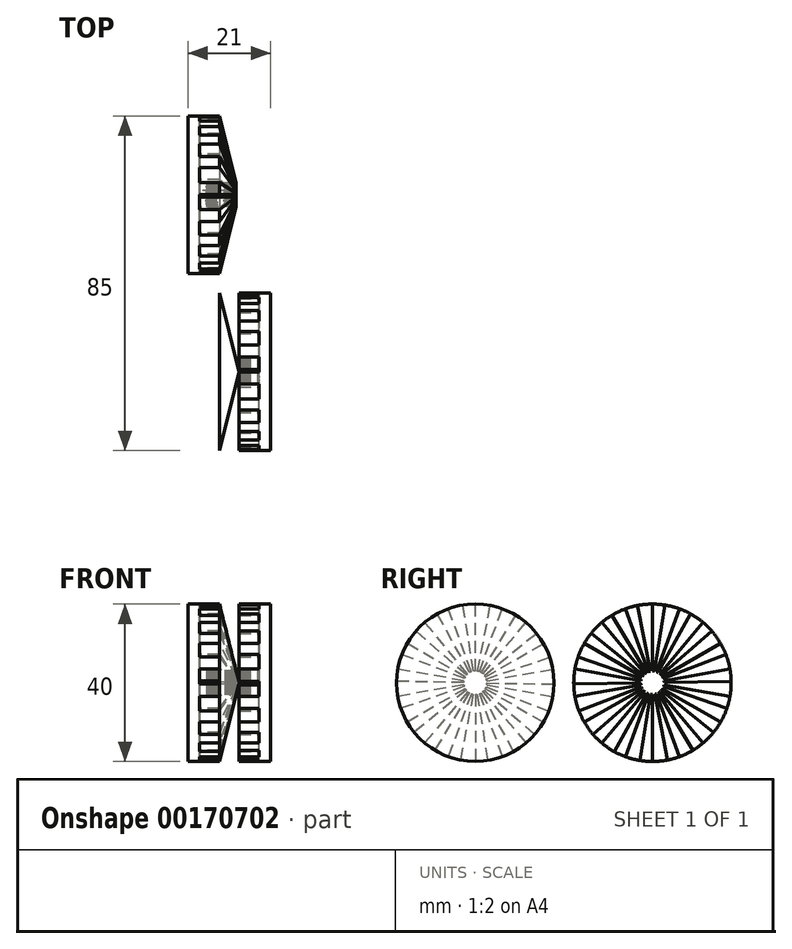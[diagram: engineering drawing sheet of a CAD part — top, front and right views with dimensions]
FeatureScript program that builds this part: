
annotation { "Feature Type Name" : "Feature", "Feature Type Description" : "" }
export const myFeature = defineFeature(function(context is Context, id is Id, definition is map)
    precondition{}
    {
        {
            var Q0;
            Q0=qCreatedBy(makeId("Front.planeOp"),FACE);
            var sketch = newSketch(context, id + "F0", { "sketchPlane" : qUnion([Q0])});
            skLineSegment(sketch, "E0", {"start": v(0, 20) * mm, "end": v(0, 0) * mm});
            skLineSegment(sketch, "E1", {"start": v(0, 0) * mm, "end": v(10, 0) * mm});
            skLineSegment(sketch, "E2", {"start": v(10, 0) * mm, "end": v(5, 20) * mm});
            skLineSegment(sketch, "E3", {"start": v(5, 20) * mm, "end": v(0, 20) * mm});
            skLineSegment(sketch, "E4", {"start": v(5, 20) * mm, "end": v(5, 0) * mm, "construction": true});
            skSolve(sketch);
        }
        {
            var Q0;
            Q0 = qSketchRegion(id + "F0", true);
            var Q1;
            Q1=sQuery(id+"F0.wireOp",EDGE,"E1");
            revolve(context, id + "F1", {"entities" : qUnion([Q0]), "axis" : qUnion([Q1]), "revolveType" : RevolveType.FULL});
        }
        {
            var Q0;
            Q0=qCreatedBy(makeId("Front.planeOp"),FACE);
            cPlane(context, id + "F2", {"entities" : qUnion([Q0]), "cplaneType" : CPlaneType.OFFSET, "offset" : 45 * mm, "width" : 150 * mm, "height" : 150 * mm});
        }
        {
            var Q0;
            Q0=qCreatedBy(id+"F2.planeOp",FACE);
            var sketch = newSketch(context, id + "F3", { "sketchPlane" : qUnion([Q0])});
            skLineSegment(sketch, "E5", {"start": v(15, 0) * mm, "end": v(15, 20) * mm});
            skLineSegment(sketch, "E6", {"start": v(15, 20) * mm, "end": v(10, 20) * mm});
            skLineSegment(sketch, "E7", {"start": v(0, 0) * mm, "end": v(5, 0) * mm, "construction": true});
            skLineSegment(sketch, "E8", {"start": v(5, 0) * mm, "end": v(10, 0) * mm});
            skLineSegment(sketch, "E9", {"start": v(10, 0) * mm, "end": v(15, 0) * mm});
            skLineSegment(sketch, "E10", {"start": v(5, 0) * mm, "end": v(5, 20) * mm});
            skLineSegment(sketch, "E11", {"start": v(5, 20) * mm, "end": v(10, 0) * mm});
            skLineSegment(sketch, "E12", {"start": v(10, 20) * mm, "end": v(10, 0) * mm});
            skLineSegment(sketch, "E13", {"start": v(5, 20) * mm, "end": v(10, 20) * mm, "construction": true});
            skSolve(sketch);
        }
        {
            var Q0;
            Q0=makeQuery(id+"F3.imprint","IMPRINT",FACE,{"disambiguationData":[TD([[makeQuery(id+"F3.imprint","IMPRINT",EDGE,{"derivedFrom":sQuery(id+"F3.wireOp",EDGE,"E5")}),1.0]])]});
            var Q1;
            Q1=makeQuery(id+"F3.imprint","IMPRINT",FACE,{"disambiguationData":[TD([[makeQuery(id+"F3.imprint","IMPRINT",EDGE,{"derivedFrom":sQuery(id+"F3.wireOp",EDGE,"E8")}),1.0]])]});
            var Q2;
            Q2=sQuery(id+"F3.wireOp",EDGE,"E9");
            revolve(context, id + "F4", {"entities" : qUnion([Q0, Q1]), "axis" : qUnion([Q2]), "revolveType" : RevolveType.FULL});
        }
        {
            var Q0;
            Q0=qCreatedBy(makeId("Right.planeOp"),FACE);
            var sketch = newSketch(context, id + "F5", { "sketchPlane" : qUnion([Q0])});
            skCircle(sketch, "E14", {"center": v(0, 0) * mm, "radius": 20 * mm});
            skSolve(sketch);
        }
        {
            var Q0;
            Q0 = qSketchRegion(id + "F5", true);
            extrude(context, id + "F6", {"entities" : qUnion([Q0]), "operationType" : NewBodyOperationType.ADD, "oppositeDirection" : true, "depth" : 3 * mm});
        }
        {
            var Q0;
            Q0=qCreatedBy(makeId("Right.planeOp"),FACE);
            var sketch = newSketch(context, id + "F7", { "sketchPlane" : qUnion([Q0])});
            skLineSegment(sketch, "E15", {"start": v(-3.82, 19.63) * mm, "end": v(-0.57, 2.94) * mm});
            skLineSegment(sketch, "E16", {"start": v(0, 3) * mm, "end": v(0, 20) * mm});
            skArc(sketch, "E17", {"start": v(0, 20) * mm, "mid": v(-1.92, 19.9) * mm, "end": v(-3.82, 19.63) * mm});
            skLineSegment(sketch, "E18", {"start": v(-0.57, 2.94) * mm, "end": v(0, 0) * mm, "construction": true});
            skLineSegment(sketch, "E19", {"start": v(0, 3) * mm, "end": v(0, 0) * mm, "construction": true});
            skArc(sketch, "E20", {"start": v(-0.57, 2.94) * mm, "mid": v(-0.8, 2.9) * mm, "end": v(-1.03, 2.82) * mm});
            skLineSegment(sketch, "E21", {"start": v(-1.03, 2.82) * mm, "end": v(0, 0) * mm, "construction": true});
            skArc(sketch, "E22.1.0", {"start": v(-6.84, 18.8) * mm, "mid": v(-8.61, 18.05) * mm, "end": v(-10.3, 17.14) * mm});
            skLineSegment(sketch, "E22.1.1", {"start": v(-10.3, 17.14) * mm, "end": v(-1.55, 2.57) * mm});
            skLineSegment(sketch, "E22.1.2", {"start": v(-1.03, 2.82) * mm, "end": v(-6.84, 18.8) * mm});
            skArc(sketch, "E22.1.3", {"start": v(-1.55, 2.57) * mm, "mid": v(-1.74, 2.44) * mm, "end": v(-1.93, 2.3) * mm});
            skArc(sketch, "E22.2.0", {"start": v(-12.86, 15.32) * mm, "mid": v(-14.27, 14.02) * mm, "end": v(-15.54, 12.59) * mm});
            skLineSegment(sketch, "E22.2.1", {"start": v(-15.54, 12.59) * mm, "end": v(-2.33, 1.89) * mm});
            skLineSegment(sketch, "E22.2.2", {"start": v(-1.93, 2.3) * mm, "end": v(-12.86, 15.32) * mm});
            skArc(sketch, "E22.2.3", {"start": v(-2.33, 1.89) * mm, "mid": v(-2.47, 1.7) * mm, "end": v(-2.6, 1.5) * mm});
            skArc(sketch, "E22.3.0", {"start": v(-17.32, 10) * mm, "mid": v(-18.2, 8.3) * mm, "end": v(-18.91, 6.51) * mm});
            skLineSegment(sketch, "E22.3.1", {"start": v(-18.91, 6.51) * mm, "end": v(-2.84, 0.98) * mm});
            skLineSegment(sketch, "E22.3.2", {"start": v(-2.6, 1.5) * mm, "end": v(-17.32, 10) * mm});
            skArc(sketch, "E22.3.3", {"start": v(-2.84, 0.98) * mm, "mid": v(-2.9, 0.75) * mm, "end": v(-2.95, 0.52) * mm});
            skArc(sketch, "E22.4.0", {"start": v(-19.7, 3.47) * mm, "mid": v(-19.94, 1.57) * mm, "end": v(-20, -0.35) * mm});
            skLineSegment(sketch, "E22.4.1", {"start": v(-20, -0.35) * mm, "end": v(-3, -0.05) * mm});
            skLineSegment(sketch, "E22.4.2", {"start": v(-2.95, 0.52) * mm, "end": v(-19.7, 3.47) * mm});
            skArc(sketch, "E22.4.3", {"start": v(-3, -0.05) * mm, "mid": v(-2.99, -0.29) * mm, "end": v(-2.95, -0.52) * mm});
            skArc(sketch, "E22.5.0", {"start": v(-19.7, -3.47) * mm, "mid": v(-19.27, -5.34) * mm, "end": v(-18.67, -7.17) * mm});
            skLineSegment(sketch, "E22.5.1", {"start": v(-18.67, -7.17) * mm, "end": v(-2.8, -1.08) * mm});
            skLineSegment(sketch, "E22.5.2", {"start": v(-2.95, -0.52) * mm, "end": v(-19.7, -3.47) * mm});
            skArc(sketch, "E22.5.3", {"start": v(-2.8, -1.08) * mm, "mid": v(-2.7, -1.3) * mm, "end": v(-2.6, -1.5) * mm});
            skArc(sketch, "E22.6.0", {"start": v(-17.32, -10) * mm, "mid": v(-16.28, -11.61) * mm, "end": v(-15.1, -13.12) * mm});
            skLineSegment(sketch, "E22.6.1", {"start": v(-15.1, -13.12) * mm, "end": v(-2.26, -1.97) * mm});
            skLineSegment(sketch, "E22.6.2", {"start": v(-2.6, -1.5) * mm, "end": v(-17.32, -10) * mm});
            skArc(sketch, "E22.6.3", {"start": v(-2.26, -1.97) * mm, "mid": v(-2.1, -2.14) * mm, "end": v(-1.93, -2.3) * mm});
            skArc(sketch, "E22.7.0", {"start": v(-12.86, -15.32) * mm, "mid": v(-11.33, -16.48) * mm, "end": v(-9.7, -17.5) * mm});
            skLineSegment(sketch, "E22.7.1", {"start": v(-9.7, -17.5) * mm, "end": v(-1.45, -2.62) * mm});
            skLineSegment(sketch, "E22.7.2", {"start": v(-1.93, -2.3) * mm, "end": v(-12.86, -15.32) * mm});
            skArc(sketch, "E22.7.3", {"start": v(-1.45, -2.62) * mm, "mid": v(-1.24, -2.73) * mm, "end": v(-1.03, -2.82) * mm});
            skArc(sketch, "E22.8.0", {"start": v(-6.84, -18.8) * mm, "mid": v(-5, -19.36) * mm, "end": v(-3.13, -19.75) * mm});
            skLineSegment(sketch, "E22.8.1", {"start": v(-3.13, -19.75) * mm, "end": v(-0.47, -2.96) * mm});
            skLineSegment(sketch, "E22.8.2", {"start": v(-1.03, -2.82) * mm, "end": v(-6.84, -18.8) * mm});
            skArc(sketch, "E22.8.3", {"start": v(-0.47, -2.96) * mm, "mid": v(-0.24, -3) * mm, "end": v(0, -3) * mm});
            skArc(sketch, "E22.9.0", {"start": v(0, -20) * mm, "mid": v(1.92, -19.9) * mm, "end": v(3.82, -19.63) * mm});
            skLineSegment(sketch, "E22.9.1", {"start": v(3.82, -19.63) * mm, "end": v(0.57, -2.94) * mm});
            skLineSegment(sketch, "E22.9.2", {"start": v(0, -3) * mm, "end": v(0, -20) * mm});
            skArc(sketch, "E22.9.3", {"start": v(0.57, -2.94) * mm, "mid": v(0.8, -2.9) * mm, "end": v(1.03, -2.82) * mm});
            skArc(sketch, "E22.10.0", {"start": v(6.84, -18.8) * mm, "mid": v(8.61, -18.05) * mm, "end": v(10.3, -17.14) * mm});
            skLineSegment(sketch, "E22.10.1", {"start": v(10.3, -17.14) * mm, "end": v(1.55, -2.57) * mm});
            skLineSegment(sketch, "E22.10.2", {"start": v(1.03, -2.82) * mm, "end": v(6.84, -18.8) * mm});
            skArc(sketch, "E22.10.3", {"start": v(1.55, -2.57) * mm, "mid": v(1.74, -2.44) * mm, "end": v(1.93, -2.3) * mm});
            skArc(sketch, "E22.11.0", {"start": v(12.86, -15.32) * mm, "mid": v(14.27, -14.02) * mm, "end": v(15.54, -12.59) * mm});
            skLineSegment(sketch, "E22.11.1", {"start": v(15.54, -12.59) * mm, "end": v(2.33, -1.89) * mm});
            skLineSegment(sketch, "E22.11.2", {"start": v(1.93, -2.3) * mm, "end": v(12.86, -15.32) * mm});
            skArc(sketch, "E22.11.3", {"start": v(2.33, -1.89) * mm, "mid": v(2.47, -1.7) * mm, "end": v(2.6, -1.5) * mm});
            skArc(sketch, "E22.12.0", {"start": v(17.32, -10) * mm, "mid": v(18.2, -8.3) * mm, "end": v(18.91, -6.51) * mm});
            skLineSegment(sketch, "E22.12.1", {"start": v(18.91, -6.51) * mm, "end": v(2.84, -0.98) * mm});
            skLineSegment(sketch, "E22.12.2", {"start": v(2.6, -1.5) * mm, "end": v(17.32, -10) * mm});
            skArc(sketch, "E22.12.3", {"start": v(2.84, -0.98) * mm, "mid": v(2.9, -0.75) * mm, "end": v(2.95, -0.52) * mm});
            skArc(sketch, "E22.13.0", {"start": v(19.7, -3.47) * mm, "mid": v(19.94, -1.57) * mm, "end": v(20, 0.35) * mm});
            skLineSegment(sketch, "E22.13.1", {"start": v(20, 0.35) * mm, "end": v(3, 0.05) * mm});
            skLineSegment(sketch, "E22.13.2", {"start": v(2.95, -0.52) * mm, "end": v(19.7, -3.47) * mm});
            skArc(sketch, "E22.13.3", {"start": v(3, 0.05) * mm, "mid": v(2.99, 0.29) * mm, "end": v(2.95, 0.52) * mm});
            skArc(sketch, "E22.14.0", {"start": v(19.7, 3.47) * mm, "mid": v(19.27, 5.34) * mm, "end": v(18.67, 7.17) * mm});
            skLineSegment(sketch, "E22.14.1", {"start": v(18.67, 7.17) * mm, "end": v(2.8, 1.08) * mm});
            skLineSegment(sketch, "E22.14.2", {"start": v(2.95, 0.52) * mm, "end": v(19.7, 3.47) * mm});
            skArc(sketch, "E22.14.3", {"start": v(2.8, 1.08) * mm, "mid": v(2.7, 1.3) * mm, "end": v(2.6, 1.5) * mm});
            skArc(sketch, "E22.15.0", {"start": v(17.32, 10) * mm, "mid": v(16.28, 11.61) * mm, "end": v(15.1, 13.12) * mm});
            skLineSegment(sketch, "E22.15.1", {"start": v(15.1, 13.12) * mm, "end": v(2.26, 1.97) * mm});
            skLineSegment(sketch, "E22.15.2", {"start": v(2.6, 1.5) * mm, "end": v(17.32, 10) * mm});
            skArc(sketch, "E22.15.3", {"start": v(2.26, 1.97) * mm, "mid": v(2.1, 2.14) * mm, "end": v(1.93, 2.3) * mm});
            skArc(sketch, "E22.16.0", {"start": v(12.86, 15.32) * mm, "mid": v(11.33, 16.48) * mm, "end": v(9.7, 17.5) * mm});
            skLineSegment(sketch, "E22.16.1", {"start": v(9.7, 17.5) * mm, "end": v(1.45, 2.62) * mm});
            skLineSegment(sketch, "E22.16.2", {"start": v(1.93, 2.3) * mm, "end": v(12.86, 15.32) * mm});
            skArc(sketch, "E22.16.3", {"start": v(1.45, 2.62) * mm, "mid": v(1.24, 2.73) * mm, "end": v(1.03, 2.82) * mm});
            skArc(sketch, "E22.17.0", {"start": v(6.84, 18.8) * mm, "mid": v(5, 19.36) * mm, "end": v(3.13, 19.75) * mm});
            skLineSegment(sketch, "E22.17.1", {"start": v(3.13, 19.75) * mm, "end": v(0.47, 2.96) * mm});
            skLineSegment(sketch, "E22.17.2", {"start": v(1.03, 2.82) * mm, "end": v(6.84, 18.8) * mm});
            skArc(sketch, "E22.17.3", {"start": v(0.47, 2.96) * mm, "mid": v(0.24, 3) * mm, "end": v(0, 3) * mm});
            skSolve(sketch);
        }
        {
            var Q0;
            Q0 = qSketchRegion(id + "F7", true);
            extrude(context, id + "F8", {"entities" : qUnion([Q0]), "operationType" : NewBodyOperationType.REMOVE, "endBound" : BoundingType.UP_TO_NEXT, "depth" : 25 * mm});
        }
        {
            var Q0;
            Q0=makeQuery(id+"F4.opRevolve","SWEPT_FACE",FACE,{"disambiguationData":[OSD([sQuery(id+"F3.wireOp",EDGE,"E5")])]});
            cPlane(context, id + "F9", {"entities" : qUnion([Q0]), "cplaneType" : CPlaneType.OFFSET, "offset" : 0 * mm, "width" : 150 * mm, "height" : 150 * mm});
        }
        {
            var Q0;
            Q0=qCreatedBy(id+"F9.planeOp",FACE);
            var sketch = newSketch(context, id + "F10", { "sketchPlane" : qUnion([Q0])});
            skCircle(sketch, "E23", {"center": v(-45, 0) * mm, "radius": 20 * mm});
            skSolve(sketch);
        }
        {
            var Q0;
            Q0 = qSketchRegion(id + "F10", true);
            extrude(context, id + "F11", {"entities" : qUnion([Q0]), "operationType" : NewBodyOperationType.ADD, "depth" : 3 * mm});
        }
        {
            var Q0;
            Q0=qCreatedBy(id+"F9.planeOp",FACE);
            var sketch = newSketch(context, id + "F12", { "sketchPlane" : qUnion([Q0])});
            skLineSegment(sketch, "E24", {"start": v(-41.18, 19.63) * mm, "end": v(-44.43, 2.94) * mm});
            skLineSegment(sketch, "E25", {"start": v(-45, 20) * mm, "end": v(-45, 3) * mm});
            skArc(sketch, "E26", {"start": v(-41.18, 19.63) * mm, "mid": v(-43.08, 19.9) * mm, "end": v(-45, 20) * mm});
            skArc(sketch, "E27", {"start": v(-43.97, 2.82) * mm, "mid": v(-44.2, 2.9) * mm, "end": v(-44.43, 2.94) * mm});
            skLineSegment(sketch, "E28", {"start": v(-43.97, 2.82) * mm, "end": v(-45, 0) * mm, "construction": true});
            skLineSegment(sketch, "E29", {"start": v(-44.43, 2.94) * mm, "end": v(-45, 0) * mm, "construction": true});
            skLineSegment(sketch, "E30", {"start": v(-45, 3) * mm, "end": v(-45, 0) * mm, "construction": true});
            skLineSegment(sketch, "E31.1.0", {"start": v(-51.84, 18.8) * mm, "end": v(-46.03, 2.82) * mm});
            skArc(sketch, "E31.1.1", {"start": v(-48.13, 19.75) * mm, "mid": v(-50, 19.36) * mm, "end": v(-51.84, 18.8) * mm});
            skLineSegment(sketch, "E31.1.2", {"start": v(-48.13, 19.75) * mm, "end": v(-45.47, 2.96) * mm});
            skArc(sketch, "E31.1.3", {"start": v(-45, 3) * mm, "mid": v(-45.24, 3) * mm, "end": v(-45.47, 2.96) * mm});
            skLineSegment(sketch, "E31.2.0", {"start": v(-57.86, 15.32) * mm, "end": v(-46.93, 2.3) * mm});
            skArc(sketch, "E31.2.1", {"start": v(-54.7, 17.5) * mm, "mid": v(-56.33, 16.48) * mm, "end": v(-57.86, 15.32) * mm});
            skLineSegment(sketch, "E31.2.2", {"start": v(-54.7, 17.5) * mm, "end": v(-46.45, 2.62) * mm});
            skArc(sketch, "E31.2.3", {"start": v(-46.03, 2.82) * mm, "mid": v(-46.24, 2.73) * mm, "end": v(-46.45, 2.62) * mm});
            skLineSegment(sketch, "E31.3.0", {"start": v(-62.32, 10) * mm, "end": v(-47.6, 1.5) * mm});
            skArc(sketch, "E31.3.1", {"start": v(-60.1, 13.12) * mm, "mid": v(-61.28, 11.61) * mm, "end": v(-62.32, 10) * mm});
            skLineSegment(sketch, "E31.3.2", {"start": v(-60.1, 13.12) * mm, "end": v(-47.26, 1.97) * mm});
            skArc(sketch, "E31.3.3", {"start": v(-46.93, 2.3) * mm, "mid": v(-47.1, 2.14) * mm, "end": v(-47.26, 1.97) * mm});
            skLineSegment(sketch, "E31.4.0", {"start": v(-64.7, 3.47) * mm, "end": v(-47.95, 0.52) * mm});
            skArc(sketch, "E31.4.1", {"start": v(-63.67, 7.17) * mm, "mid": v(-64.27, 5.34) * mm, "end": v(-64.7, 3.47) * mm});
            skLineSegment(sketch, "E31.4.2", {"start": v(-63.67, 7.17) * mm, "end": v(-47.8, 1.08) * mm});
            skArc(sketch, "E31.4.3", {"start": v(-47.6, 1.5) * mm, "mid": v(-47.7, 1.3) * mm, "end": v(-47.8, 1.08) * mm});
            skLineSegment(sketch, "E31.5.0", {"start": v(-64.7, -3.47) * mm, "end": v(-47.95, -0.52) * mm});
            skArc(sketch, "E31.5.1", {"start": v(-65, 0.35) * mm, "mid": v(-64.94, -1.57) * mm, "end": v(-64.7, -3.47) * mm});
            skLineSegment(sketch, "E31.5.2", {"start": v(-65, 0.35) * mm, "end": v(-48, 0.05) * mm});
            skArc(sketch, "E31.5.3", {"start": v(-47.95, 0.52) * mm, "mid": v(-47.99, 0.29) * mm, "end": v(-48, 0.05) * mm});
            skLineSegment(sketch, "E31.6.0", {"start": v(-62.32, -10) * mm, "end": v(-47.6, -1.5) * mm});
            skArc(sketch, "E31.6.1", {"start": v(-63.91, -6.51) * mm, "mid": v(-63.2, -8.3) * mm, "end": v(-62.32, -10) * mm});
            skLineSegment(sketch, "E31.6.2", {"start": v(-63.91, -6.51) * mm, "end": v(-47.84, -0.98) * mm});
            skArc(sketch, "E31.6.3", {"start": v(-47.95, -0.52) * mm, "mid": v(-47.9, -0.75) * mm, "end": v(-47.84, -0.98) * mm});
            skLineSegment(sketch, "E31.7.0", {"start": v(-57.86, -15.32) * mm, "end": v(-46.93, -2.3) * mm});
            skArc(sketch, "E31.7.1", {"start": v(-60.54, -12.59) * mm, "mid": v(-59.27, -14.02) * mm, "end": v(-57.86, -15.32) * mm});
            skLineSegment(sketch, "E31.7.2", {"start": v(-60.54, -12.59) * mm, "end": v(-47.33, -1.89) * mm});
            skArc(sketch, "E31.7.3", {"start": v(-47.6, -1.5) * mm, "mid": v(-47.47, -1.7) * mm, "end": v(-47.33, -1.89) * mm});
            skLineSegment(sketch, "E31.8.0", {"start": v(-51.84, -18.8) * mm, "end": v(-46.03, -2.82) * mm});
            skArc(sketch, "E31.8.1", {"start": v(-55.3, -17.14) * mm, "mid": v(-53.61, -18.05) * mm, "end": v(-51.84, -18.8) * mm});
            skLineSegment(sketch, "E31.8.2", {"start": v(-55.3, -17.14) * mm, "end": v(-46.55, -2.57) * mm});
            skArc(sketch, "E31.8.3", {"start": v(-46.93, -2.3) * mm, "mid": v(-46.74, -2.44) * mm, "end": v(-46.55, -2.57) * mm});
            skLineSegment(sketch, "E31.9.0", {"start": v(-45, -20) * mm, "end": v(-45, -3) * mm});
            skArc(sketch, "E31.9.1", {"start": v(-48.82, -19.63) * mm, "mid": v(-46.92, -19.9) * mm, "end": v(-45, -20) * mm});
            skLineSegment(sketch, "E31.9.2", {"start": v(-48.82, -19.63) * mm, "end": v(-45.57, -2.94) * mm});
            skArc(sketch, "E31.9.3", {"start": v(-46.03, -2.82) * mm, "mid": v(-45.8, -2.9) * mm, "end": v(-45.57, -2.94) * mm});
            skLineSegment(sketch, "E31.10.0", {"start": v(-38.16, -18.8) * mm, "end": v(-43.97, -2.82) * mm});
            skArc(sketch, "E31.10.1", {"start": v(-41.87, -19.75) * mm, "mid": v(-40, -19.36) * mm, "end": v(-38.16, -18.8) * mm});
            skLineSegment(sketch, "E31.10.2", {"start": v(-41.87, -19.75) * mm, "end": v(-44.53, -2.96) * mm});
            skArc(sketch, "E31.10.3", {"start": v(-45, -3) * mm, "mid": v(-44.76, -3) * mm, "end": v(-44.53, -2.96) * mm});
            skLineSegment(sketch, "E31.11.0", {"start": v(-32.14, -15.32) * mm, "end": v(-43.07, -2.3) * mm});
            skArc(sketch, "E31.11.1", {"start": v(-35.3, -17.5) * mm, "mid": v(-33.67, -16.48) * mm, "end": v(-32.14, -15.32) * mm});
            skLineSegment(sketch, "E31.11.2", {"start": v(-35.3, -17.5) * mm, "end": v(-43.55, -2.62) * mm});
            skArc(sketch, "E31.11.3", {"start": v(-43.97, -2.82) * mm, "mid": v(-43.76, -2.73) * mm, "end": v(-43.55, -2.62) * mm});
            skLineSegment(sketch, "E31.12.0", {"start": v(-27.68, -10) * mm, "end": v(-42.4, -1.5) * mm});
            skArc(sketch, "E31.12.1", {"start": v(-29.9, -13.12) * mm, "mid": v(-28.72, -11.61) * mm, "end": v(-27.68, -10) * mm});
            skLineSegment(sketch, "E31.12.2", {"start": v(-29.9, -13.12) * mm, "end": v(-42.74, -1.97) * mm});
            skArc(sketch, "E31.12.3", {"start": v(-43.07, -2.3) * mm, "mid": v(-42.9, -2.14) * mm, "end": v(-42.74, -1.97) * mm});
            skLineSegment(sketch, "E31.13.0", {"start": v(-25.3, -3.47) * mm, "end": v(-42.05, -0.52) * mm});
            skArc(sketch, "E31.13.1", {"start": v(-26.33, -7.17) * mm, "mid": v(-25.73, -5.34) * mm, "end": v(-25.3, -3.47) * mm});
            skLineSegment(sketch, "E31.13.2", {"start": v(-26.33, -7.17) * mm, "end": v(-42.2, -1.08) * mm});
            skArc(sketch, "E31.13.3", {"start": v(-42.4, -1.5) * mm, "mid": v(-42.3, -1.3) * mm, "end": v(-42.2, -1.08) * mm});
            skLineSegment(sketch, "E31.14.0", {"start": v(-25.3, 3.47) * mm, "end": v(-42.05, 0.52) * mm});
            skArc(sketch, "E31.14.1", {"start": v(-25, -0.35) * mm, "mid": v(-25.06, 1.57) * mm, "end": v(-25.3, 3.47) * mm});
            skLineSegment(sketch, "E31.14.2", {"start": v(-25, -0.35) * mm, "end": v(-42, -0.05) * mm});
            skArc(sketch, "E31.14.3", {"start": v(-42.05, -0.52) * mm, "mid": v(-42.01, -0.29) * mm, "end": v(-42, -0.05) * mm});
            skLineSegment(sketch, "E31.15.0", {"start": v(-27.68, 10) * mm, "end": v(-42.4, 1.5) * mm});
            skArc(sketch, "E31.15.1", {"start": v(-26.09, 6.51) * mm, "mid": v(-26.8, 8.3) * mm, "end": v(-27.68, 10) * mm});
            skLineSegment(sketch, "E31.15.2", {"start": v(-26.09, 6.51) * mm, "end": v(-42.16, 0.98) * mm});
            skArc(sketch, "E31.15.3", {"start": v(-42.05, 0.52) * mm, "mid": v(-42.1, 0.75) * mm, "end": v(-42.16, 0.98) * mm});
            skLineSegment(sketch, "E31.16.0", {"start": v(-32.14, 15.32) * mm, "end": v(-43.07, 2.3) * mm});
            skArc(sketch, "E31.16.1", {"start": v(-29.46, 12.59) * mm, "mid": v(-30.73, 14.02) * mm, "end": v(-32.14, 15.32) * mm});
            skLineSegment(sketch, "E31.16.2", {"start": v(-29.46, 12.59) * mm, "end": v(-42.67, 1.89) * mm});
            skArc(sketch, "E31.16.3", {"start": v(-42.4, 1.5) * mm, "mid": v(-42.53, 1.7) * mm, "end": v(-42.67, 1.89) * mm});
            skLineSegment(sketch, "E31.17.0", {"start": v(-38.16, 18.8) * mm, "end": v(-43.97, 2.82) * mm});
            skArc(sketch, "E31.17.1", {"start": v(-34.7, 17.14) * mm, "mid": v(-36.39, 18.05) * mm, "end": v(-38.16, 18.8) * mm});
            skLineSegment(sketch, "E31.17.2", {"start": v(-34.7, 17.14) * mm, "end": v(-43.45, 2.57) * mm});
            skArc(sketch, "E31.17.3", {"start": v(-43.07, 2.3) * mm, "mid": v(-43.26, 2.44) * mm, "end": v(-43.45, 2.57) * mm});
            skSolve(sketch);
        }
        {
            var Q0;
            Q0 = qSketchRegion(id + "F12", true);
            extrude(context, id + "F13", {"entities" : qUnion([Q0]), "operationType" : NewBodyOperationType.REMOVE, "endBound" : BoundingType.UP_TO_NEXT, "oppositeDirection" : true, "depth" : 25 * mm});
        }
    });
